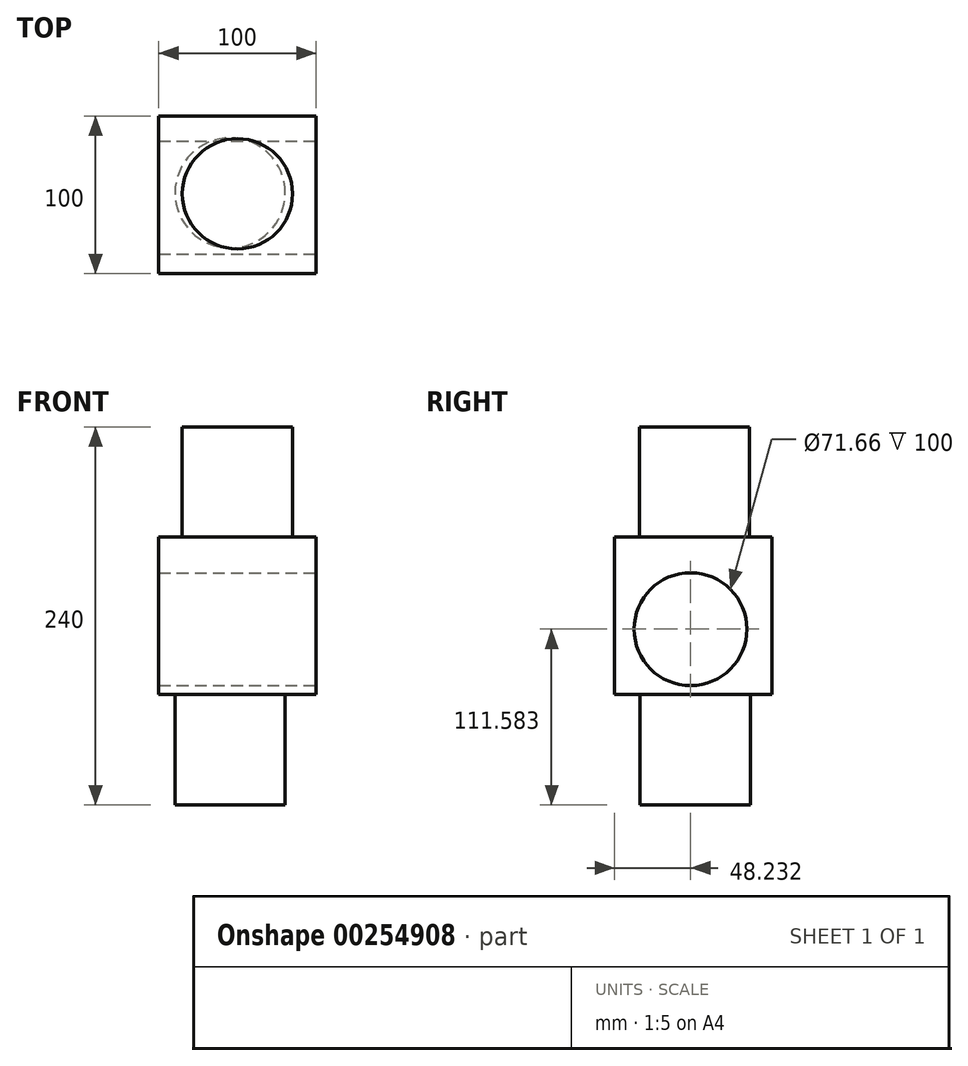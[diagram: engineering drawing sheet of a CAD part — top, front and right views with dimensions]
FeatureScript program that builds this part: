
annotation { "Feature Type Name" : "Feature", "Feature Type Description" : "" }
export const myFeature = defineFeature(function(context is Context, id is Id, definition is map)
    precondition{}
    {
        {
            var Q0;
            Q0=qCreatedBy(makeId("Front.planeOp"),FACE);
            var sketch = newSketch(context, id + "F0", { "sketchPlane" : qUnion([Q0])});
            skLineSegment(sketch, "E0.bottom", {"start": v(0, 0) * mm, "end": v(100, 0) * mm});
            skLineSegment(sketch, "E0.top", {"start": v(0, 100) * mm, "end": v(100, 100) * mm});
            skLineSegment(sketch, "E0.left", {"start": v(0, 0) * mm, "end": v(0, 100) * mm});
            skLineSegment(sketch, "E0.right", {"start": v(100, 0) * mm, "end": v(100, 100) * mm});
            skSolve(sketch);
        }
        {
            var Q0;
            Q0 = qSketchRegion(id + "F0", true);
            extrude(context, id + "F1", {"entities" : qUnion([Q0]), "depth" : 100 * mm});
        }
        {
            var Q0;
            Q0=makeQuery(id+"F1.opExtrude","SWEPT_FACE",FACE,{"disambiguationData":[OSD([sQuery(id+"F0.wireOp",EDGE,"E0.top")])]});
            var sketch = newSketch(context, id + "F2", { "sketchPlane" : qUnion([Q0])});
            skCircle(sketch, "E1", {"center": v(50, -49.38) * mm, "radius": 35 * mm});
            skSolve(sketch);
        }
        {
            var Q0;
            Q0 = qSketchRegion(id + "F2", true);
            extrude(context, id + "F3", {"entities" : qUnion([Q0]), "operationType" : NewBodyOperationType.ADD, "depth" : 70 * mm});
        }
        {
            var Q0;
            Q0=makeQuery(id+"F1.opExtrude","SWEPT_FACE",FACE,{"disambiguationData":[OSD([sQuery(id+"F0.wireOp",EDGE,"E0.bottom")])]});
            var sketch = newSketch(context, id + "F4", { "sketchPlane" : qUnion([Q0])});
            skCircle(sketch, "E2", {"center": v(45.4, 48.76) * mm, "radius": 35 * mm});
            skSolve(sketch);
        }
        {
            var Q0;
            Q0 = qSketchRegion(id + "F4", true);
            extrude(context, id + "F5", {"entities" : qUnion([Q0]), "operationType" : NewBodyOperationType.ADD, "depth" : 70 * mm});
        }
        {
            var Q0;
            Q0=makeQuery(id+"F1.opExtrude","SWEPT_FACE",FACE,{"disambiguationData":[OSD([sQuery(id+"F0.wireOp",EDGE,"E0.right")])]});
            var sketch = newSketch(context, id + "F6", { "sketchPlane" : qUnion([Q0])});
            skCircle(sketch, "E3", {"center": v(-51.77, 41.58) * mm, "radius": 35.83 * mm});
            skPoint(sketch, "E4", {"position": v(-20.51, 59.1) * mm});
            skPoint(sketch, "E5", {"position": v(-40.97, 75.75) * mm});
            skPoint(sketch, "E6", {"position": v(-50, 5.8) * mm});
            skPoint(sketch, "E6.positionSnap0", {"position": v(-50, 0) * mm});
            skSolve(sketch);
        }
        {
            var Q0;
            Q0=makeQuery(id+"F6.imprint","IMPRINT",FACE,{"disambiguationData":[TD([[makeQuery(id+"F6.imprint","IMPRINT",EDGE,{"derivedFrom":sQuery(id+"F6.wireOp",EDGE,"E3")}),1.0]])]});
            extrude(context, id + "F7", {"entities" : qUnion([Q0]), "operationType" : NewBodyOperationType.REMOVE, "endBound" : BoundingType.THROUGH_ALL, "oppositeDirection" : true, "depth" : 25 * mm});
        }
    });
